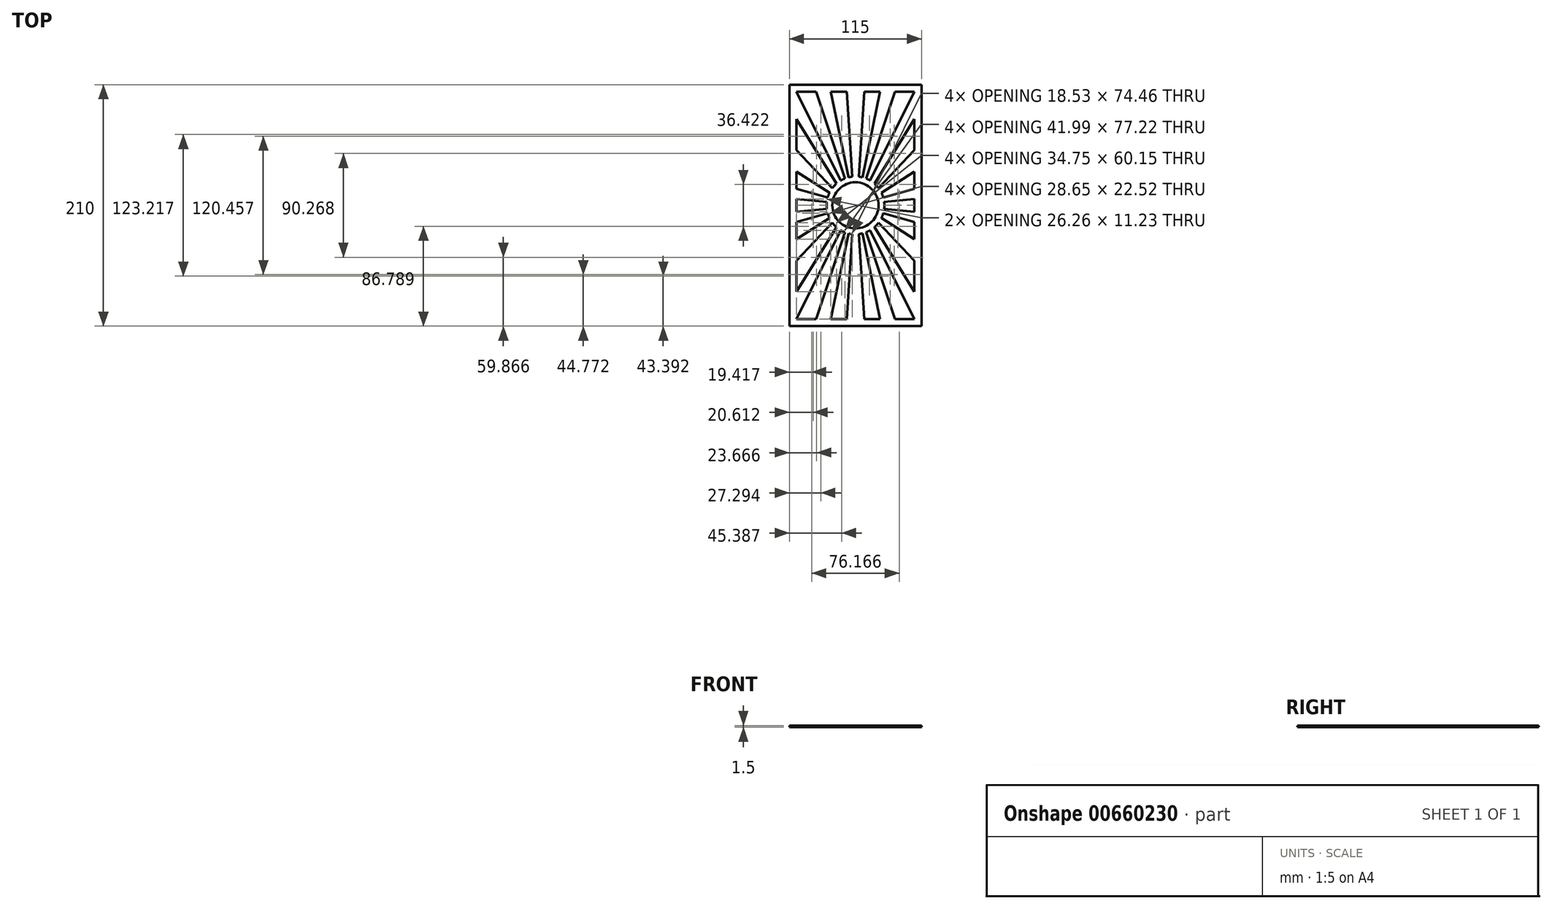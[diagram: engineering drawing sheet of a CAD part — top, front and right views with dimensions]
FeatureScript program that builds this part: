
annotation { "Feature Type Name" : "Feature", "Feature Type Description" : "" }
export const myFeature = defineFeature(function(context is Context, id is Id, definition is map)
    precondition{}
    {
        {
            var Q0;
            Q0=qCreatedBy(makeId("Top.planeOp"),FACE);
            var sketch = newSketch(context, id + "F0", { "sketchPlane" : qUnion([Q0])});
            skLineSegment(sketch, "E0.bottom", {"start": v(57.5, -105) * mm, "end": v(-57.5, -105) * mm});
            skLineSegment(sketch, "E0.top", {"start": v(57.5, 105) * mm, "end": v(-57.5, 105) * mm});
            skLineSegment(sketch, "E0.left", {"start": v(57.5, -105) * mm, "end": v(57.5, 105) * mm});
            skLineSegment(sketch, "E0.right", {"start": v(-57.5, -105) * mm, "end": v(-57.5, 105) * mm});
            skCircle(sketch, "E1", {"center": v(0, 0) * mm, "radius": 20.1 * mm});
            skLineSegment(sketch, "E2.MirrorCS", {"start": v(-22.56, -11.05) * mm, "end": v(-51.21, -29.47) * mm});
            skLineSegment(sketch, "E3.MirrorCS", {"start": v(-12.8, -21.62) * mm, "end": v(-51.2, -98.84) * mm});
            skLineSegment(sketch, "E4.MirrorCS", {"start": v(-24.14, -6.95) * mm, "end": v(-51.21, -14.36) * mm});
            skLineSegment(sketch, "E5.MirrorCS", {"start": v(-6.07, -24.38) * mm, "end": v(-21.38, -98.84) * mm});
            skLineSegment(sketch, "E6.MirrorCS", {"start": v(-9.2, -23.37) * mm, "end": v(-34.33, -98.84) * mm});
            skLineSegment(sketch, "E7.MirrorCS", {"start": v(-16.46, -18.98) * mm, "end": v(-51.2, -75.21) * mm});
            skLineSegment(sketch, "E8.MirrorCS", {"start": v(-24.95, -2.91) * mm, "end": v(-51.21, -5.61) * mm});
            skLineSegment(sketch, "E9.MirrorCS", {"start": v(-20.1, -15.06) * mm, "end": v(-51.2, -48.05) * mm});
            skLineSegment(sketch, "E10.MirrorCS", {"start": v(-2.85, -24.96) * mm, "end": v(-7.68, -98.84) * mm});
            skLineSegment(sketch, "E11", {"start": v(-7.68, -98.84) * mm, "end": v(-21.38, -98.84) * mm});
            skLineSegment(sketch, "E12", {"start": v(-34.33, -98.84) * mm, "end": v(-51.2, -98.84) * mm});
            skLineSegment(sketch, "E13", {"start": v(-51.21, 5.61) * mm, "end": v(-51.21, -5.61) * mm});
            skLineSegment(sketch, "E14", {"start": v(-51.21, -14.36) * mm, "end": v(-51.21, -29.47) * mm});
            skLineSegment(sketch, "E15", {"start": v(-51.2, -48.05) * mm, "end": v(-51.2, -75.21) * mm});
            skArc(sketch, "E16", {"start": v(-2.85, -24.96) * mm, "mid": v(-4.47, -24.72) * mm, "end": v(-6.07, -24.38) * mm});
            skArc(sketch, "E17", {"start": v(-9.2, -23.37) * mm, "mid": v(-11.04, -22.57) * mm, "end": v(-12.8, -21.62) * mm});
            skArc(sketch, "E18", {"start": v(-16.46, -18.98) * mm, "mid": v(-18.39, -17.12) * mm, "end": v(-20.1, -15.06) * mm});
            skArc(sketch, "E19", {"start": v(-22.56, -11.05) * mm, "mid": v(-23.44, -9.03) * mm, "end": v(-24.14, -6.95) * mm});
            skArc(sketch, "E20", {"start": v(-24.95, -2.91) * mm, "mid": v(-25.12, 0) * mm, "end": v(-24.95, 2.91) * mm});
            skArc(sketch, "E21.MirrorCS", {"start": v(-9.2, 23.37) * mm, "mid": v(-11.04, 22.57) * mm, "end": v(-12.8, 21.62) * mm});
            skArc(sketch, "E22.MirrorCS", {"start": v(-16.46, 18.98) * mm, "mid": v(-18.39, 17.12) * mm, "end": v(-20.1, 15.06) * mm});
            skArc(sketch, "E23.MirrorCS", {"start": v(-2.85, 24.96) * mm, "mid": v(-4.47, 24.72) * mm, "end": v(-6.07, 24.38) * mm});
            skArc(sketch, "E24.MirrorCS", {"start": v(-22.56, 11.05) * mm, "mid": v(-23.44, 9.03) * mm, "end": v(-24.14, 6.95) * mm});
            skLineSegment(sketch, "E25.MirrorCS", {"start": v(-51.21, 14.36) * mm, "end": v(-51.21, 29.47) * mm});
            skLineSegment(sketch, "E26.MirrorCS", {"start": v(-7.68, 98.84) * mm, "end": v(-21.38, 98.84) * mm});
            skLineSegment(sketch, "E27.MirrorCS", {"start": v(-12.8, 21.62) * mm, "end": v(-51.2, 98.84) * mm});
            skLineSegment(sketch, "E28.MirrorCS", {"start": v(-6.07, 24.38) * mm, "end": v(-21.38, 98.84) * mm});
            skLineSegment(sketch, "E29.MirrorCS", {"start": v(-24.95, 2.91) * mm, "end": v(-51.21, 5.61) * mm});
            skLineSegment(sketch, "E30.MirrorCS", {"start": v(-9.2, 23.37) * mm, "end": v(-34.33, 98.84) * mm});
            skLineSegment(sketch, "E31.MirrorCS", {"start": v(-22.56, 11.05) * mm, "end": v(-51.21, 29.47) * mm});
            skLineSegment(sketch, "E32.MirrorCS", {"start": v(-16.46, 18.98) * mm, "end": v(-51.2, 75.21) * mm});
            skLineSegment(sketch, "E33.MirrorCS", {"start": v(-2.85, 24.96) * mm, "end": v(-7.68, 98.84) * mm});
            skLineSegment(sketch, "E34.MirrorCS", {"start": v(-24.14, 6.95) * mm, "end": v(-51.21, 14.36) * mm});
            skArc(sketch, "E35.MirrorCS", {"start": v(-24.95, 2.91) * mm, "mid": v(-25.12, 0) * mm, "end": v(-24.95, -2.91) * mm});
            skLineSegment(sketch, "E36.MirrorCS", {"start": v(-34.33, 98.84) * mm, "end": v(-51.2, 98.84) * mm});
            skLineSegment(sketch, "E37.MirrorCS", {"start": v(-20.1, 15.06) * mm, "end": v(-51.2, 48.05) * mm});
            skLineSegment(sketch, "E38.MirrorCS", {"start": v(-51.2, 48.05) * mm, "end": v(-51.2, 75.21) * mm});
            skArc(sketch, "E39.MirrorCS", {"start": v(24.95, 2.91) * mm, "mid": v(25.12, 0) * mm, "end": v(24.95, -2.91) * mm});
            skArc(sketch, "E40.MirrorCS", {"start": v(24.95, -2.91) * mm, "mid": v(25.12, 0) * mm, "end": v(24.95, 2.91) * mm});
            skArc(sketch, "E41.MirrorCS", {"start": v(9.2, -23.37) * mm, "mid": v(11.04, -22.57) * mm, "end": v(12.8, -21.62) * mm});
            skArc(sketch, "E42.MirrorCS", {"start": v(2.85, 24.96) * mm, "mid": v(4.47, 24.72) * mm, "end": v(6.07, 24.38) * mm});
            skArc(sketch, "E43.MirrorCS", {"start": v(9.2, 23.37) * mm, "mid": v(11.04, 22.57) * mm, "end": v(12.8, 21.62) * mm});
            skArc(sketch, "E44.MirrorCS", {"start": v(16.46, -18.98) * mm, "mid": v(18.39, -17.12) * mm, "end": v(20.1, -15.06) * mm});
            skArc(sketch, "E45.MirrorCS", {"start": v(2.85, -24.96) * mm, "mid": v(4.47, -24.72) * mm, "end": v(6.07, -24.38) * mm});
            skArc(sketch, "E46.MirrorCS", {"start": v(22.56, -11.05) * mm, "mid": v(23.44, -9.03) * mm, "end": v(24.14, -6.95) * mm});
            skArc(sketch, "E47.MirrorCS", {"start": v(16.46, 18.98) * mm, "mid": v(18.39, 17.12) * mm, "end": v(20.1, 15.06) * mm});
            skArc(sketch, "E48.MirrorCS", {"start": v(22.56, 11.05) * mm, "mid": v(23.44, 9.03) * mm, "end": v(24.14, 6.95) * mm});
            skLineSegment(sketch, "E49.MirrorCS", {"start": v(12.8, 21.62) * mm, "end": v(51.2, 98.84) * mm});
            skLineSegment(sketch, "E50.MirrorCS", {"start": v(16.46, 18.98) * mm, "end": v(51.2, 75.21) * mm});
            skLineSegment(sketch, "E51.MirrorCS", {"start": v(12.8, -21.62) * mm, "end": v(51.2, -98.84) * mm});
            skLineSegment(sketch, "E52.MirrorCS", {"start": v(22.56, 11.05) * mm, "end": v(51.21, 29.47) * mm});
            skLineSegment(sketch, "E53.MirrorCS", {"start": v(34.33, -98.84) * mm, "end": v(51.2, -98.84) * mm});
            skLineSegment(sketch, "E54.MirrorCS", {"start": v(20.1, -15.06) * mm, "end": v(51.2, -48.05) * mm});
            skLineSegment(sketch, "E55.MirrorCS", {"start": v(7.68, -98.84) * mm, "end": v(21.38, -98.84) * mm});
            skLineSegment(sketch, "E56.MirrorCS", {"start": v(7.68, 98.84) * mm, "end": v(21.38, 98.84) * mm});
            skLineSegment(sketch, "E57.MirrorCS", {"start": v(2.85, -24.96) * mm, "end": v(7.68, -98.84) * mm});
            skLineSegment(sketch, "E58.MirrorCS", {"start": v(24.14, 6.95) * mm, "end": v(51.21, 14.36) * mm});
            skLineSegment(sketch, "E59.MirrorCS", {"start": v(24.95, -2.91) * mm, "end": v(51.21, -5.61) * mm});
            skLineSegment(sketch, "E60.MirrorCS", {"start": v(16.46, -18.98) * mm, "end": v(51.2, -75.21) * mm});
            skLineSegment(sketch, "E61.MirrorCS", {"start": v(51.2, -48.05) * mm, "end": v(51.2, -75.21) * mm});
            skLineSegment(sketch, "E62.MirrorCS", {"start": v(24.95, 2.91) * mm, "end": v(51.21, 5.61) * mm});
            skLineSegment(sketch, "E63.MirrorCS", {"start": v(51.21, 14.36) * mm, "end": v(51.21, 29.47) * mm});
            skLineSegment(sketch, "E64.MirrorCS", {"start": v(51.21, -14.36) * mm, "end": v(51.21, -29.47) * mm});
            skLineSegment(sketch, "E65.MirrorCS", {"start": v(34.33, 98.84) * mm, "end": v(51.2, 98.84) * mm});
            skLineSegment(sketch, "E66.MirrorCS", {"start": v(6.07, 24.38) * mm, "end": v(21.38, 98.84) * mm});
            skLineSegment(sketch, "E67.MirrorCS", {"start": v(20.1, 15.06) * mm, "end": v(51.2, 48.05) * mm});
            skLineSegment(sketch, "E68.MirrorCS", {"start": v(22.56, -11.05) * mm, "end": v(51.21, -29.47) * mm});
            skLineSegment(sketch, "E69.MirrorCS", {"start": v(51.2, 48.05) * mm, "end": v(51.2, 75.21) * mm});
            skLineSegment(sketch, "E70.MirrorCS", {"start": v(9.2, -23.37) * mm, "end": v(34.33, -98.84) * mm});
            skLineSegment(sketch, "E71.MirrorCS", {"start": v(6.07, -24.38) * mm, "end": v(21.38, -98.84) * mm});
            skLineSegment(sketch, "E72.MirrorCS", {"start": v(24.14, -6.95) * mm, "end": v(51.21, -14.36) * mm});
            skLineSegment(sketch, "E73.MirrorCS", {"start": v(51.21, 5.61) * mm, "end": v(51.21, -5.61) * mm});
            skLineSegment(sketch, "E74.MirrorCS", {"start": v(9.2, 23.37) * mm, "end": v(34.33, 98.84) * mm});
            skLineSegment(sketch, "E75.MirrorCS", {"start": v(2.85, 24.96) * mm, "end": v(7.68, 98.84) * mm});
            skSolve(sketch);
        }
        {
            var Q0;
            Q0 = qSketchRegion(id + "F0", true);
            extrude(context, id + "F1", {"entities" : qUnion([Q0]), "depth" : 1.5 * mm, "offsetDistance" : 25 * mm});
        }
    });
